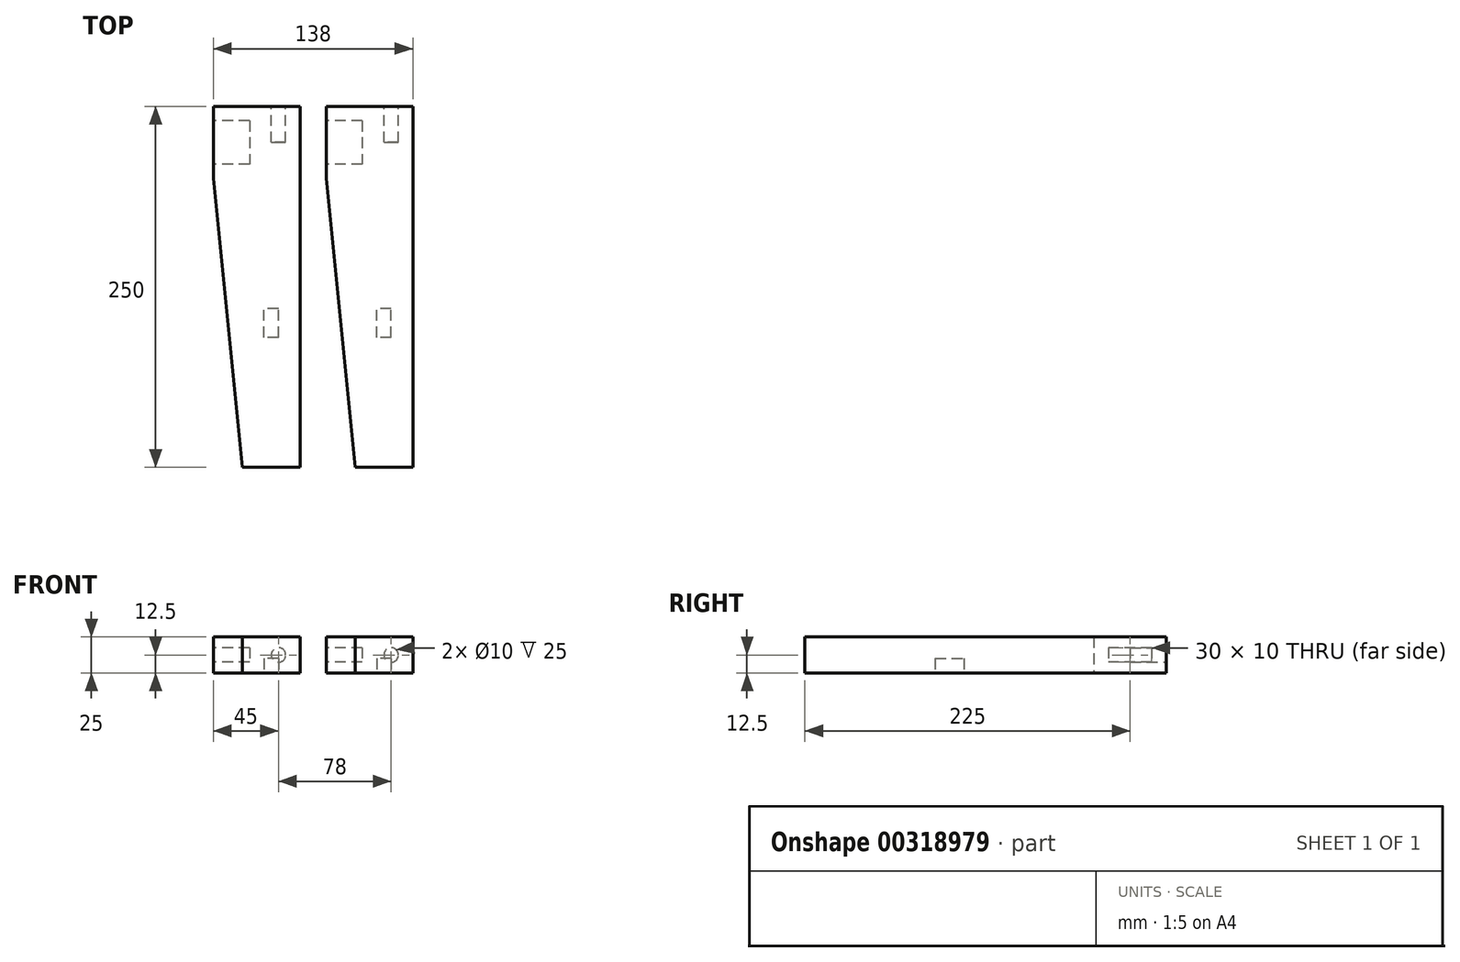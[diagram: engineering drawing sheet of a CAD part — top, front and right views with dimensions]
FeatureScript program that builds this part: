
annotation { "Feature Type Name" : "Feature", "Feature Type Description" : "" }
export const myFeature = defineFeature(function(context is Context, id is Id, definition is map)
    precondition{}
    {
        {
            var Q0;
            Q0=qCreatedBy(makeId("Top.planeOp"),FACE);
            var sketch = newSketch(context, id + "F0", { "sketchPlane" : qUnion([Q0])});
            skLineSegment(sketch, "E0.bottom", {"start": v(30, 125) * mm, "end": v(-30, 125) * mm});
            skLineSegment(sketch, "E0.left", {"start": v(30, 125) * mm, "end": v(30, -125) * mm});
            skPoint(sketch, "E0.middle", {"position": v(0, 0) * mm});
            skLineSegment(sketch, "E1", {"start": v(-30, 125) * mm, "end": v(-30, 75) * mm});
            skLineSegment(sketch, "E2", {"start": v(-30, 75) * mm, "end": v(-10, -125) * mm});
            skLineSegment(sketch, "E3", {"start": v(30, -125) * mm, "end": v(-10, -125) * mm});
            skSolve(sketch);
        }
        {
            var Q0;
            Q0 = qSketchRegion(id + "F0", true);
            extrude(context, id + "F1", {"entities" : qUnion([Q0]), "depth" : 25 * mm});
        }
        {
            var Q0;
            Q0=makeQuery(id+"F1.opExtrude","SWEPT_FACE",FACE,{"disambiguationData":[OSD([sQuery(id+"F0.wireOp",EDGE,"E1")])]});
            var sketch = newSketch(context, id + "F2", { "sketchPlane" : qUnion([Q0])});
            skLineSegment(sketch, "E4", {"start": v(-125, 17.5) * mm, "end": v(-115, 17.5) * mm, "construction": true});
            skLineSegment(sketch, "E5", {"start": v(-115, 17.5) * mm, "end": v(-115, 25) * mm, "construction": true});
            skLineSegment(sketch, "E6.bottom", {"start": v(-115, 17.5) * mm, "end": v(-85, 17.5) * mm});
            skLineSegment(sketch, "E6.top", {"start": v(-115, 7.5) * mm, "end": v(-85, 7.5) * mm});
            skLineSegment(sketch, "E6.left", {"start": v(-115, 17.5) * mm, "end": v(-115, 7.5) * mm});
            skLineSegment(sketch, "E6.right", {"start": v(-85, 17.5) * mm, "end": v(-85, 7.5) * mm});
            skSolve(sketch);
        }
        {
            var Q0;
            Q0 = qSketchRegion(id + "F2", true);
            extrude(context, id + "F3", {"entities" : qUnion([Q0]), "operationType" : NewBodyOperationType.REMOVE, "oppositeDirection" : true, "depth" : 25 * mm});
        }
        {
            var Q0;
            Q0=makeQuery(id+"F1.opExtrude","SWEPT_FACE",FACE,{"disambiguationData":[OSD([sQuery(id+"F0.wireOp",EDGE,"E0.bottom")])]});
            var sketch = newSketch(context, id + "F4", { "sketchPlane" : qUnion([Q0])});
            skLineSegment(sketch, "E7", {"start": v(-30, 12.5) * mm, "end": v(-15, 12.5) * mm, "construction": true});
            skLineSegment(sketch, "E8", {"start": v(-15, 12.5) * mm, "end": v(30, 12.5) * mm, "construction": true});
            skCircle(sketch, "E9", {"center": v(-15, 12.5) * mm, "radius": 5 * mm});
            skSolve(sketch);
        }
        {
            var Q0;
            Q0 = qSketchRegion(id + "F4", true);
            extrude(context, id + "F5", {"entities" : qUnion([Q0]), "operationType" : NewBodyOperationType.REMOVE, "oppositeDirection" : true, "depth" : 25 * mm});
        }
        {
            var Q0;
            Q0=makeQuery(id+"F1.opExtrude","CAP_FACE",FACE,{"disambiguationData":[OSD([sQuery(id+"F0.wireOp",EDGE,"E0.bottom"),sQuery(id+"F0.wireOp",EDGE,"E0.left"),sQuery(id+"F0.wireOp",EDGE,"E1"),sQuery(id+"F0.wireOp",EDGE,"E2"),sQuery(id+"F0.wireOp",EDGE,"E3")])],"isStart":true});
            var sketch = newSketch(context, id + "F6", { "sketchPlane" : qUnion([Q0])});
            skLineSegment(sketch, "E10", {"start": v(15, 125) * mm, "end": v(15, 35) * mm, "construction": true});
            skLineSegment(sketch, "E11", {"start": v(15, 35) * mm, "end": v(30, 35) * mm, "construction": true});
            skLineSegment(sketch, "E12.bottom", {"start": v(15, 35) * mm, "end": v(5, 35) * mm});
            skLineSegment(sketch, "E12.top", {"start": v(15, 15) * mm, "end": v(5, 15) * mm});
            skLineSegment(sketch, "E12.left", {"start": v(15, 35) * mm, "end": v(15, 15) * mm});
            skLineSegment(sketch, "E12.right", {"start": v(5, 35) * mm, "end": v(5, 15) * mm});
            skSolve(sketch);
        }
        {
            var Q0;
            Q0 = qSketchRegion(id + "F6", true);
            extrude(context, id + "F7", {"entities" : qUnion([Q0]), "operationType" : NewBodyOperationType.REMOVE, "oppositeDirection" : true, "depth" : 10 * mm});
        }
        {
            var Q0;
            Q0=makeQuery(id+"F1.opExtrude","SWEPT_BODY",BODY,{"disambiguationData":[OSD([sQuery(id+"F0.wireOp",EDGE,"E0.bottom"),sQuery(id+"F0.wireOp",EDGE,"E0.left"),sQuery(id+"F0.wireOp",EDGE,"E1"),sQuery(id+"F0.wireOp",EDGE,"E2"),sQuery(id+"F0.wireOp",EDGE,"E3")])]});
            transform(context, id + "F8", {"entities" : qUnion([Q0]), "transformType" : TransformType.TRANSLATION_3D, "dx" : 78 * mm, "dy" : 0 * mm, "dz" : 0 * mm, "makeCopy" : true});
        }
    });
